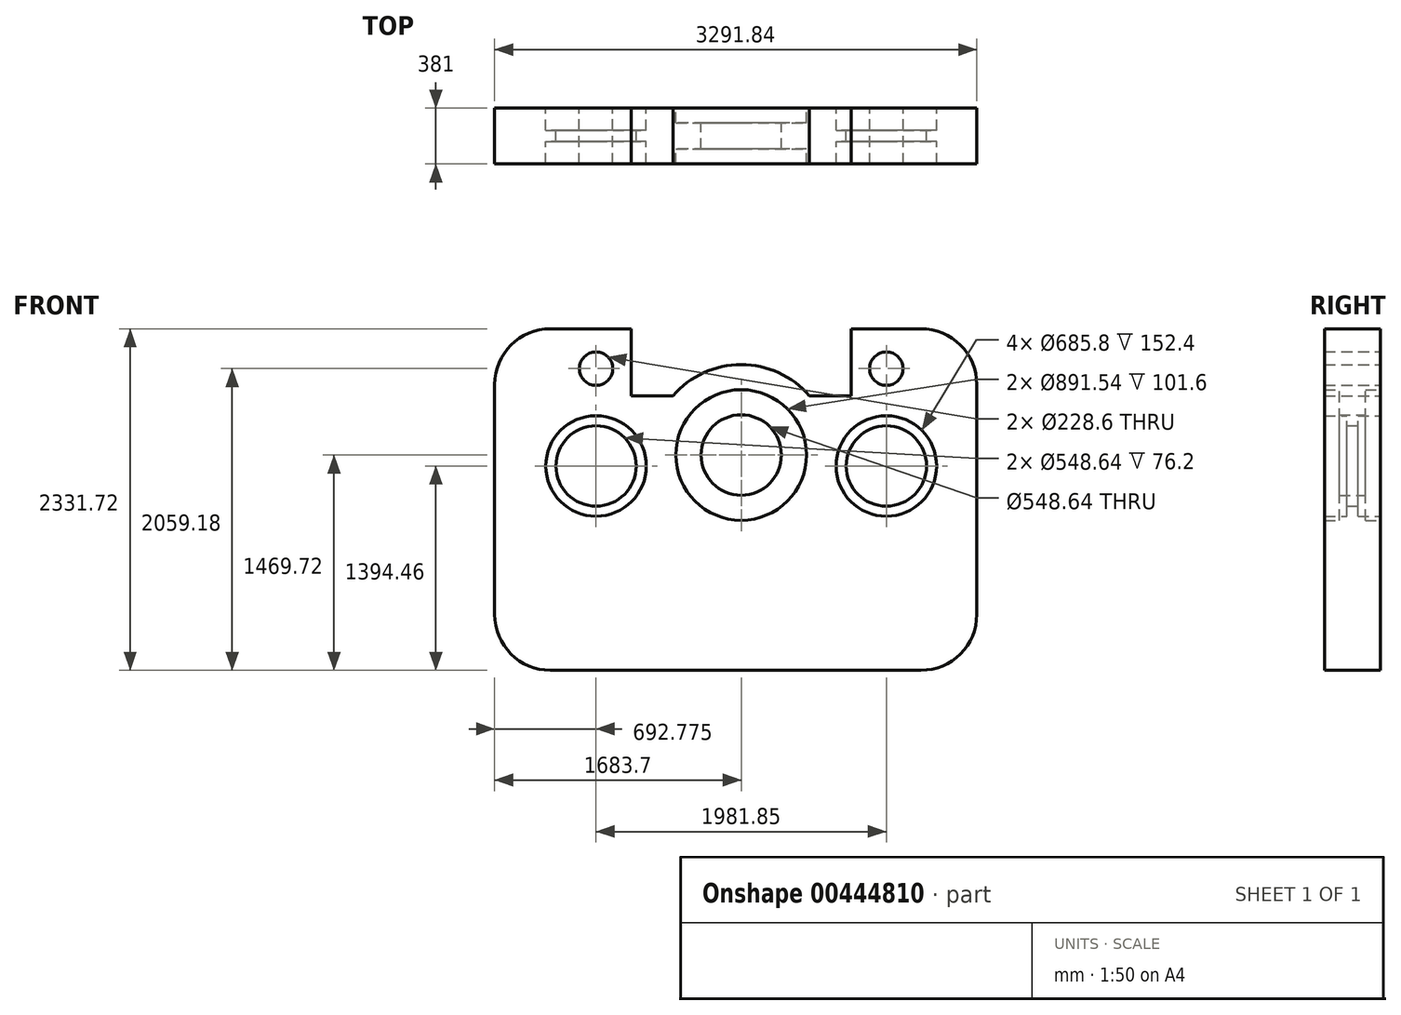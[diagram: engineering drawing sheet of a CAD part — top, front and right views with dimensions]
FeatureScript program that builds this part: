
annotation { "Feature Type Name" : "Feature", "Feature Type Description" : "" }
export const myFeature = defineFeature(function(context is Context, id is Id, definition is map)
    precondition{}
    {
        {
            var Q0;
            Q0=qCreatedBy(makeId("Front.planeOp"),FACE);
            var sketch = newSketch(context, id + "F0", { "sketchPlane" : qUnion([Q0])});
            skLineSegment(sketch, "E0", {"start": v(0, 0) * mm, "end": v(0, -457.2) * mm});
            skLineSegment(sketch, "E1", {"start": v(0, 0) * mm, "end": v(476.25, 0) * mm});
            skLineSegment(sketch, "E2", {"start": v(857.25, -381) * mm, "end": v(857.25, -1950.72) * mm});
            skLineSegment(sketch, "E3", {"start": v(476.25, -2331.72) * mm, "end": v(-2053.59, -2331.72) * mm});
            skLineSegment(sketch, "E4", {"start": v(-2434.6, -1950.72) * mm, "end": v(-2434.6, -381) * mm});
            skLineSegment(sketch, "E5", {"start": v(-2053.59, 0) * mm, "end": v(-1501.78, 0) * mm});
            skLineSegment(sketch, "E6", {"start": v(-1501.78, 0) * mm, "end": v(-1501.78, -457.2) * mm});
            skArc(sketch, "E7", {"start": v(-284.95, -457.2) * mm, "mid": v(-750.9, -244.78) * mm, "end": v(-1216.83, -457.2) * mm});
            skLineSegment(sketch, "E8", {"start": v(-1501.78, -457.2) * mm, "end": v(-1216.83, -457.2) * mm});
            skLineSegment(sketch, "E9", {"start": v(0, -457.2) * mm, "end": v(-284.95, -457.2) * mm});
            skCircle(sketch, "E10", {"center": v(-750.9, -862) * mm, "radius": 274.32 * mm});
            skCircle(sketch, "E11", {"center": v(-750.9, -862) * mm, "radius": 445.77 * mm});
            skCircle(sketch, "E12", {"center": v(-1741.81, -937.26) * mm, "radius": 342.9 * mm});
            skCircle(sketch, "E13", {"center": v(-1741.81, -272.54) * mm, "radius": 114.3 * mm});
            skCircle(sketch, "E14", {"center": v(240.03, -272.54) * mm, "radius": 114.3 * mm});
            skPoint(sketch, "E14.centerSnap0", {"position": v(-1501.78, -228.6) * mm});
            skCircle(sketch, "E15", {"center": v(240.03, -937.26) * mm, "radius": 342.9 * mm});
            skCircle(sketch, "E16", {"center": v(-1741.81, -937.26) * mm, "radius": 274.32 * mm});
            skCircle(sketch, "E17", {"center": v(240.03, -937.26) * mm, "radius": 274.32 * mm});
            skArc(sketch, "E18", {"start": v(-2434.59, -1950.72) * mm, "mid": v(-2323, -2220.13) * mm, "end": v(-2053.59, -2331.72) * mm});
            skArc(sketch, "E19", {"start": v(476.25, -2331.72) * mm, "mid": v(745.66, -2220.13) * mm, "end": v(857.25, -1950.72) * mm});
            skArc(sketch, "E20", {"start": v(-2053.59, 0) * mm, "mid": v(-2323, -111.6) * mm, "end": v(-2434.6, -381) * mm});
            skArc(sketch, "E21", {"start": v(857.25, -381) * mm, "mid": v(745.66, -111.6) * mm, "end": v(476.25, 0) * mm});
            skSolve(sketch);
        }
        {
            var Q0;
            Q0=makeQuery(id+"F0.imprint","IMPRINT",FACE,{"disambiguationData":[TD([[makeQuery(id+"F0.imprint","IMPRINT",EDGE,{"derivedFrom":sQuery(id+"F0.wireOp",EDGE,"E0")}),1.0]])]});
            extrude(context, id + "F1", {"entities" : qUnion([Q0]), "depth" : 381 * mm, "symmetric" : true});
        }
        {
            var Q0;
            Q0=makeQuery(id+"F0.imprint","IMPRINT",FACE,{"disambiguationData":[TD([[makeQuery(id+"F0.imprint","IMPRINT",EDGE,{"derivedFrom":sQuery(id+"F0.wireOp",EDGE,"E10")}),-1.0]])]});
            extrude(context, id + "F2", {"entities" : qUnion([Q0]), "operationType" : NewBodyOperationType.ADD, "depth" : 177.8 * mm, "symmetric" : true});
        }
        {
            var Q0;
            Q0=makeQuery(id+"F0.imprint","IMPRINT",FACE,{"disambiguationData":[TD([[makeQuery(id+"F0.imprint","IMPRINT",EDGE,{"derivedFrom":sQuery(id+"F0.wireOp",EDGE,"E12")}),1.0]])]});
            var Q1;
            Q1=makeQuery(id+"F0.imprint","IMPRINT",FACE,{"disambiguationData":[TD([[makeQuery(id+"F0.imprint","IMPRINT",EDGE,{"derivedFrom":sQuery(id+"F0.wireOp",EDGE,"E15")}),1.0]])]});
            extrude(context, id + "F3", {"entities" : qUnion([Q0, Q1]), "operationType" : NewBodyOperationType.ADD, "depth" : 76.2 * mm, "symmetric" : true});
        }
    });
